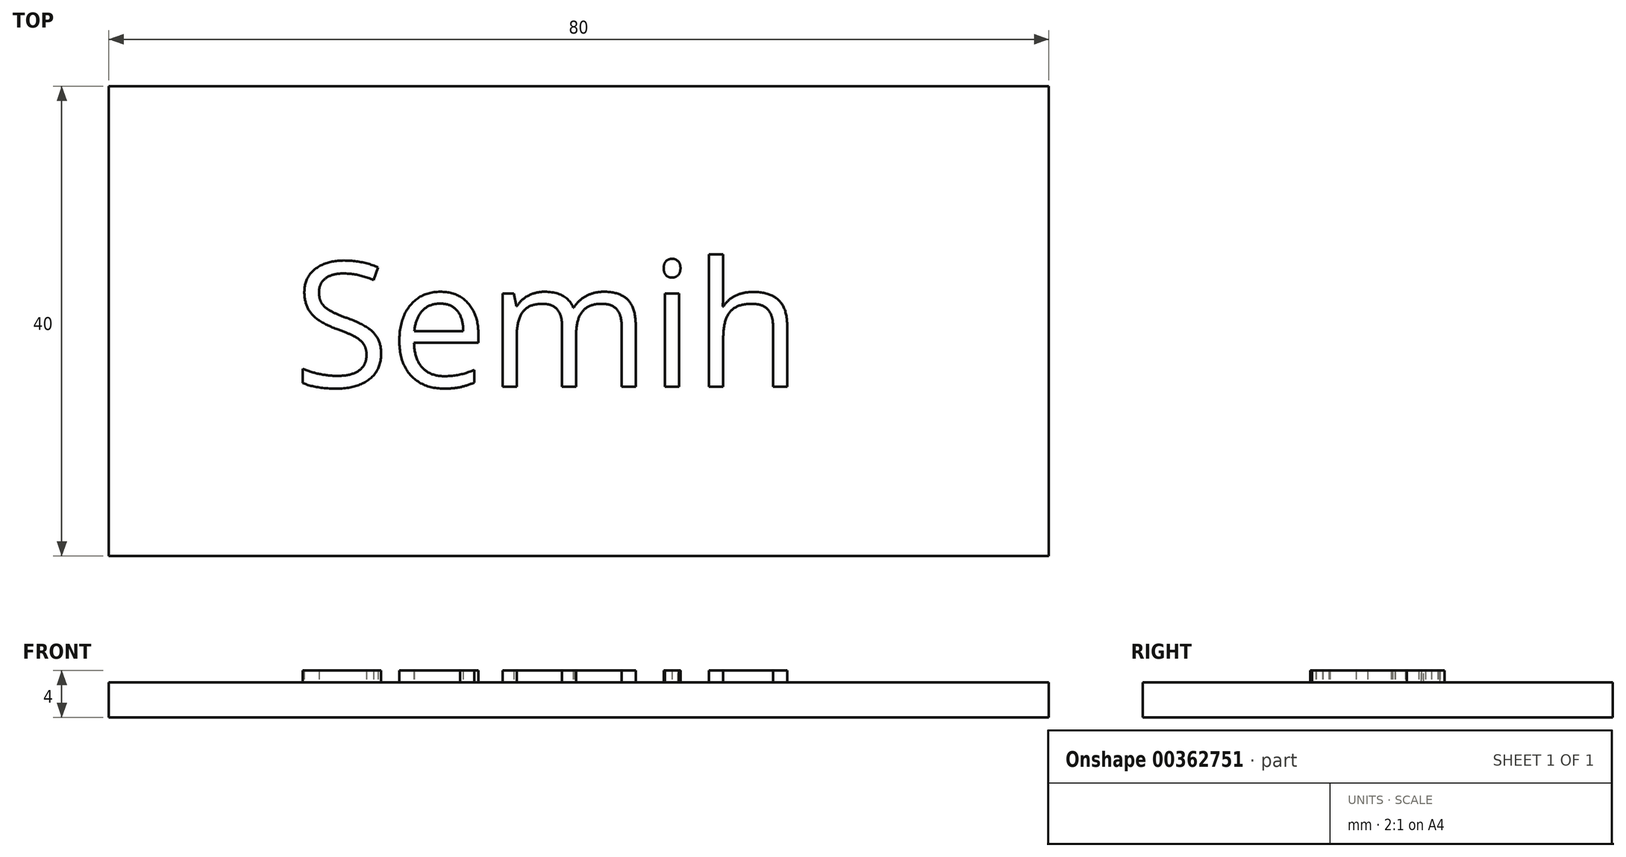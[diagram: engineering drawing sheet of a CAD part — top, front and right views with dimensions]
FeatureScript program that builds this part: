
annotation { "Feature Type Name" : "Feature", "Feature Type Description" : "" }
export const myFeature = defineFeature(function(context is Context, id is Id, definition is map)
    precondition{}
    {
        {
            var Q0;
            Q0=qCreatedBy(makeId("Top.planeOp"),FACE);
            var sketch = newSketch(context, id + "F0", { "sketchPlane" : qUnion([Q0])});
            skLineSegment(sketch, "E0.bottom", {"start": v(0, 0) * mm, "end": v(80, 0) * mm});
            skLineSegment(sketch, "E0.top", {"start": v(0, 40) * mm, "end": v(80, 40) * mm});
            skLineSegment(sketch, "E0.left", {"start": v(0, 0) * mm, "end": v(0, 40) * mm});
            skLineSegment(sketch, "E0.right", {"start": v(80, 0) * mm, "end": v(80, 40) * mm});
            skSolve(sketch);
        }
        {
            var Q0;
            Q0 = qSketchRegion(id + "F0", true);
            extrude(context, id + "F1", {"entities" : qUnion([Q0]), "depth" : 3 * mm});
        }
        {
            var Q0;
            Q0=makeQuery(id+"F1.opExtrude","CAP_FACE",FACE,{"disambiguationData":[OSD([sQuery(id+"F0.wireOp",EDGE,"E0.bottom"),sQuery(id+"F0.wireOp",EDGE,"E0.top"),sQuery(id+"F0.wireOp",EDGE,"E0.left"),sQuery(id+"F0.wireOp",EDGE,"E0.right")])],"isStart":false});
            var sketch = newSketch(context, id + "F2", { "sketchPlane" : qUnion([Q0])});
            skText(sketch, "E1", { "text": "Semih", "fontName": "OpenSans-Regular.ttf"});
            const initialGuessF2  = {"E1": [0.01573, 0.0144, 1, 0, 0.0107]};
            skSetInitialGuess(sketch, initialGuessF2);
            skSolve(sketch);
        }
        {
            var Q0;
            Q0 = qSketchRegion(id + "F2", true);
            extrude(context, id + "F3", {"entities" : qUnion([Q0]), "operationType" : NewBodyOperationType.ADD, "depth" : 1 * mm});
        }
    });
